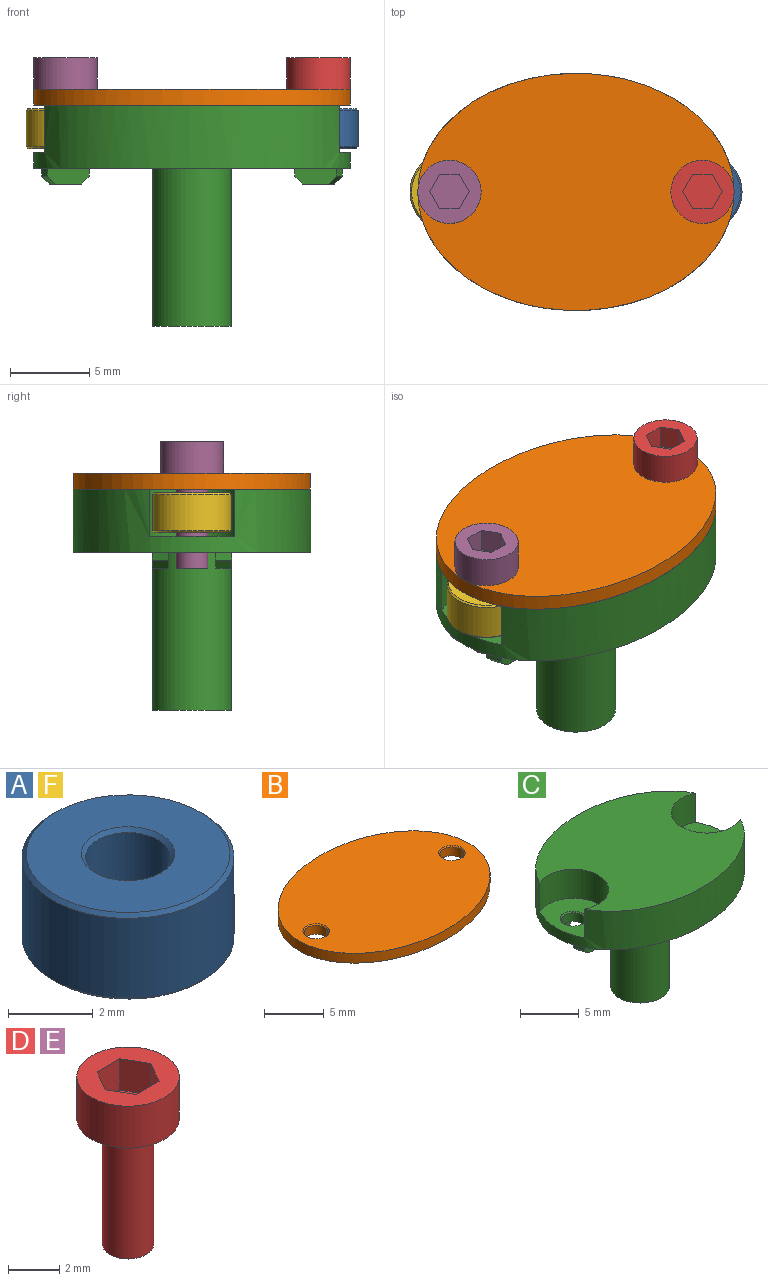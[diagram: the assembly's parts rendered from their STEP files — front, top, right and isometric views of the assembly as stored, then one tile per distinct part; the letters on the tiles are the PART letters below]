
ASSEMBLY  parts=6 mates=5
PART A: 8 faces, bbox 5x5x2.5 mm
  f0: cylinder r=1mm len=2.3mm, axis (0,0,-1), area 14.5mm2, adj f4,f5
  f1: cylinder r=2.5mm len=5mm, axis (0,0,-1), area 36.1mm2, adj f6,f7
  f2: plane 4.8x4.8mm, normal (0,0,1), area 14.3mm2, adj f5,f7
  f3: plane 4.8x4.8mm, normal (0,0,-1), area 14.3mm2, adj f4,f6
  f4: cone r=1.1mm half-angle=45deg, axis (0,0,-1), area 0.9mm2, adj f0,f3
  f5: cone r=1mm half-angle=45deg, axis (0,0,1), area 0.9mm2, adj f0,f2
  f6: cone r=2.5mm half-angle=45deg, axis (0,0,1), area 2.2mm2, adj f1,f3
  f7: cone r=2.4mm half-angle=45deg, axis (0,0,-1), area 2.2mm2, adj f1,f2
PART B: 7 faces, bbox 20x15x1 mm
  f0: extruded ~20x15mm, area 55.3mm2, adj f1,f2
  f1: plane 20x15mm, normal (0,0,1), area 228mm2, adj f0,f5,f6
  f2: plane 20x15mm, normal (0,0,-1), area 229.3mm2, adj f0,f3,f4
  f3: cylinder r=1mm len=2mm, axis (0,0,-1), area 5.7mm2, adj f2,f5
  f4: cylinder r=1mm len=2mm, axis (0,0,-1), area 5.7mm2, adj f2,f6
  f5: cone r=1.1mm half-angle=45deg, axis (0,0,1), area 0.9mm2, adj f1,f3
  f6: cone r=1.1mm half-angle=45deg, axis (0,0,1), area 0.9mm2, adj f1,f4
PART C: 41 faces, bbox 20x15x14 mm
  f0: plane 20x15mm, normal (0,0,-1), area 198.4mm2, adj f2,f3,f9,f10,f11,f12,f13,f14
  f1: plane 18.67x15mm, normal (0,0,1), area 187.1mm2, adj f2,f5,f7
  f2: extruded ~20x15mm, area 187.5mm2, adj f0,f1,f5,f6,f7,f8
  f3: cylinder r=2.5mm len=10mm, axis (0,0,1), area 157.1mm2, adj f0,f4
  f4: plane 5x5mm, normal (0,0,-1), area 19.6mm2, adj f3
  f5: cylinder r=3mm len=6mm, axis (0,0,1), area 36.6mm2, adj f1,f2,f6
  f6: plane 6x5mm, normal (0,0,1), area 20.5mm2, adj f2,f5,f39
  f7: cylinder r=3mm len=6mm, axis (0,0,1), area 36.6mm2, adj f1,f2,f8
  f8: plane 6x5mm, normal (0,0,1), area 20.5mm2, adj f2,f7,f40
  f9: cylinder r=1mm len=2mm, axis (0,0,-1), area 5.7mm2, adj f0,f40
  f10: cylinder r=1mm len=2mm, axis (0,0,-1), area 5.7mm2, adj f0,f39
  f11: plane 1x0.5mm, normal (1,0,0), area 0.5mm2, adj f0,f12,f14,f38
  f12: plane 3x1mm, normal (0,1,0), area 2.7mm2, adj f0,f11,f13,f15,f37,f38
  f13: plane 1x0.5mm, normal (-0.95,-0.32,0), area 0.5mm2, adj f0,f12,f14,f37
  f14: plane 2.66x1mm, normal (0,-1,0), area 2.4mm2, adj f0,f11,f13,f15,f37,f38
  f15: plane 1.97x1mm, normal (0,0,-1), area 1.8mm2, adj f12,f14,f37,f38
  f16: plane 3x1mm, normal (0,-1,0), area 2.7mm2, adj f0,f17,f19,f20,f35,f36
  f17: plane 1x0.5mm, normal (1,0,0), area 0.5mm2, adj f0,f16,f18,f35
  f18: plane 2.66x1mm, normal (0,1,0), area 2.4mm2, adj f0,f17,f19,f20,f35,f36
  f19: plane 1x0.5mm, normal (-0.95,0.32,0), area 0.5mm2, adj f0,f16,f18,f36
  f20: plane 1.97x1mm, normal (0,0,-1), area 1.8mm2, adj f16,f18,f35,f36
  f21: plane 1x0.5mm, normal (-1,0,0), area 0.5mm2, adj f0,f22,f24,f34
  f22: plane 2.66x1mm, normal (0,-1,0), area 2.4mm2, adj f0,f21,f23,f25,f32,f34
  f23: plane 1x0.5mm, normal (0.95,-0.32,0), area 0.5mm2, adj f0,f22,f24,f32
  f24: plane 3x1mm, normal (0,1,0), area 2.7mm2, adj f0,f21,f23,f25,f32,f34
  f25: plane 1.97x1mm, normal (0,0,-1), area 1.8mm2, adj f22,f24,f32,f34
  f26: plane 3x1mm, normal (0,-1,0), area 2.7mm2, adj f0,f27,f29,f30,f31,f33
  f27: plane 1x0.5mm, normal (0.95,0.32,0), area 0.5mm2, adj f0,f26,f28,f31
  f28: plane 2.66x1mm, normal (0,1,0), area 2.4mm2, adj f0,f27,f29,f30,f31,f33
  f29: plane 1x0.5mm, normal (-1,0,0), area 0.5mm2, adj f0,f26,f28,f33
  f30: plane 1.97x1mm, normal (0,0,-1), area 1.8mm2, adj f26,f28,f31,f33
  f31: plane 1x0.87mm, normal (0.67,0.23,-0.71), area 0.7mm2, adj f26,f27,f28,f30
  f32: plane 1x0.87mm, normal (0.67,-0.23,-0.71), area 0.7mm2, adj f22,f23,f24,f25
  f33: plane 1x0.5mm, normal (-0.71,0,-0.71), area 0.7mm2, adj f26,f28,f29,f30
  f34: plane 1x0.5mm, normal (-0.71,0,-0.71), area 0.7mm2, adj f21,f22,f24,f25
  f35: plane 1x0.5mm, normal (0.71,0,-0.71), area 0.7mm2, adj f16,f17,f18,f20
  f36: plane 1x0.87mm, normal (-0.67,0.23,-0.71), area 0.7mm2, adj f16,f18,f19,f20
  f37: plane 1x0.87mm, normal (-0.67,-0.23,-0.71), area 0.7mm2, adj f12,f13,f14,f15
  f38: plane 1x0.5mm, normal (0.71,0,-0.71), area 0.7mm2, adj f11,f12,f14,f15
  f39: cone r=1.1mm half-angle=45deg, axis (0,0,1), area 0.9mm2, adj f6,f10
  f40: cone r=1.1mm half-angle=45deg, axis (0,0,1), area 0.9mm2, adj f8,f9
PART D: 12 faces, bbox 4x4x8 mm
  f0: plane 4x4mm, normal (0,0,1), area 8.5mm2, adj f3,f5,f6,f7,f8,f9,f10
  f1: cylinder r=1mm len=6mm, axis (0,0,-1), area 37.7mm2, adj f2,f4
  f2: plane 2x2mm, normal (0,0,-1), area 3.1mm2, adj f1
  f3: cylinder r=2mm len=4mm, axis (0,0,-1), area 25.1mm2, adj f0,f4
  f4: plane 4x4mm, normal (0,0,-1), area 9.4mm2, adj f1,f3
  f5: plane 1.5x1.08mm, normal (0.87,-0.5,0), area 1.9mm2, adj f0,f6,f10,f11
  f6: plane 1.5x1.08mm, normal (0.87,0.5,0), area 1.9mm2, adj f0,f5,f7,f11
  f7: plane 1.5x1.25mm, normal (0,1,0), area 1.9mm2, adj f0,f6,f8,f11
  f8: plane 1.5x1.08mm, normal (-0.87,0.5,0), area 1.9mm2, adj f0,f7,f9,f11
  f9: plane 1.5x1.08mm, normal (-0.87,-0.5,0), area 1.9mm2, adj f0,f8,f10,f11
  f10: plane 1.5x1.25mm, normal (0,-1,0), area 1.9mm2, adj f0,f5,f9,f11
  f11: plane 2.5x2.17mm, normal (0,0,1), area 4.1mm2, adj f5,f6,f7,f8,f9,f10
PART E: same geometry as D
PART F: same geometry as A
PLACE A t=(27.89,-1.88,2.19)mm
PLACE B t=(-0.35,-1.88,0.94)mm
PLACE C t=(-0.35,-1.88,0.94)mm
PLACE D t=(35.79,-1.88,-0.06)mm
PLACE E t=(19.79,-1.88,-0.06)mm
PLACE F t=(11.89,-1.88,2.19)mm
MATE revolute A.f0 <-> D.f1  axis (0,0,-1) through (7.65,-1.88,3.44)mm
MATE fastened B.f2 <-> C.f3  axis (0,0,-1) through (-0.35,-1.88,4.94)mm
MATE revolute F.f0 <-> E.f1  axis (0,0,-1) through (-8.35,-1.88,3.44)mm
MATE fastened D.f1 <-> C.f10  axis (0,0,-1) through (7.65,-1.88,-0.06)mm
MATE fastened E.f1 <-> C.f9  axis (0,0,-1) through (-8.35,-1.88,-0.06)mm
